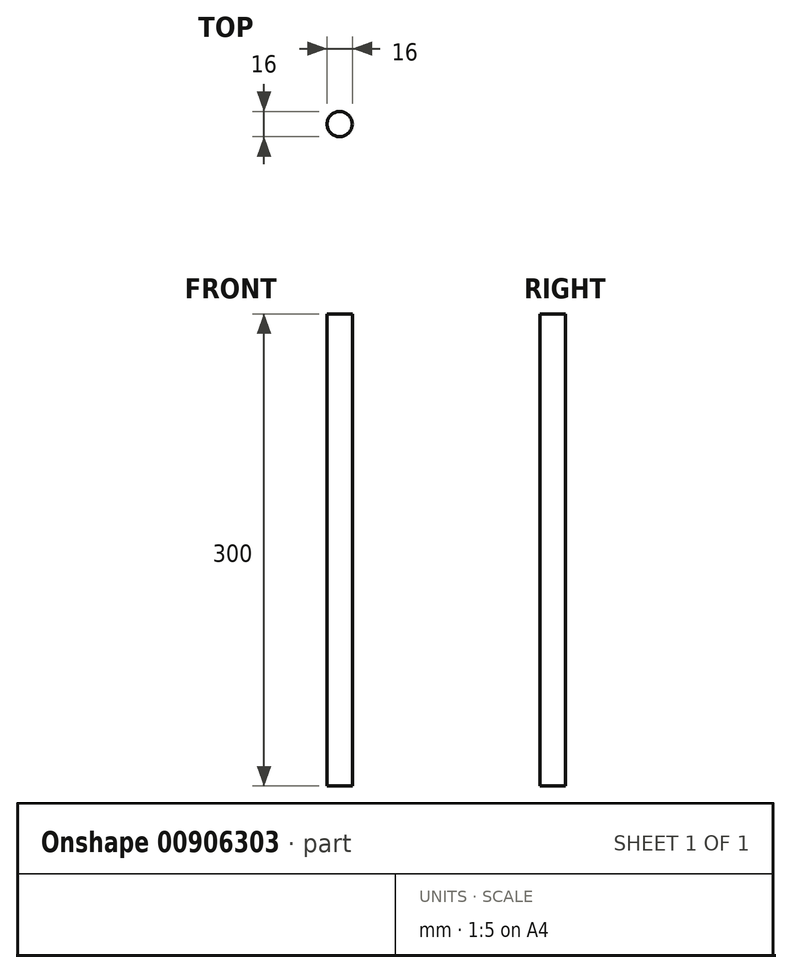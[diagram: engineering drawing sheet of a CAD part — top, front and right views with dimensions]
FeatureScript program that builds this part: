
annotation { "Feature Type Name" : "Feature", "Feature Type Description" : "" }
export const myFeature = defineFeature(function(context is Context, id is Id, definition is map)
    precondition{}
    {
        {
            var Q0;
            Q0=qCreatedBy(makeId("Top.planeOp"),FACE);
            var sketch = newSketch(context, id + "F0", { "sketchPlane" : qUnion([Q0])});
            skCircle(sketch, "E0", {"center": v(0, 0) * mm, "radius": 8 * mm});
            skSolve(sketch);
        }
        {
            var Q0;
            Q0=qCreatedBy(makeId("Front.planeOp"),FACE);
            var sketch = newSketch(context, id + "F1", { "sketchPlane" : qUnion([Q0])});
            skLineSegment(sketch, "E1", {"start": v(0, 0) * mm, "end": v(0, 300) * mm});
            skSolve(sketch);
        }
        {
            var Q0;
            Q0=makeQuery(id+"F0.imprint","IMPRINT",FACE,{"disambiguationData":[TD([[makeQuery(id+"F0.imprint","IMPRINT",EDGE,{"derivedFrom":sQuery(id+"F0.wireOp",EDGE,"E0")}),1.0]])]});
            var Q1;
            Q1=sQuery(id+"F1.wireOp",EDGE,"E1");
            sweep(context, id + "F2", {"profiles" : qUnion([Q0]), "path" : qUnion([Q1])});
        }
    });
